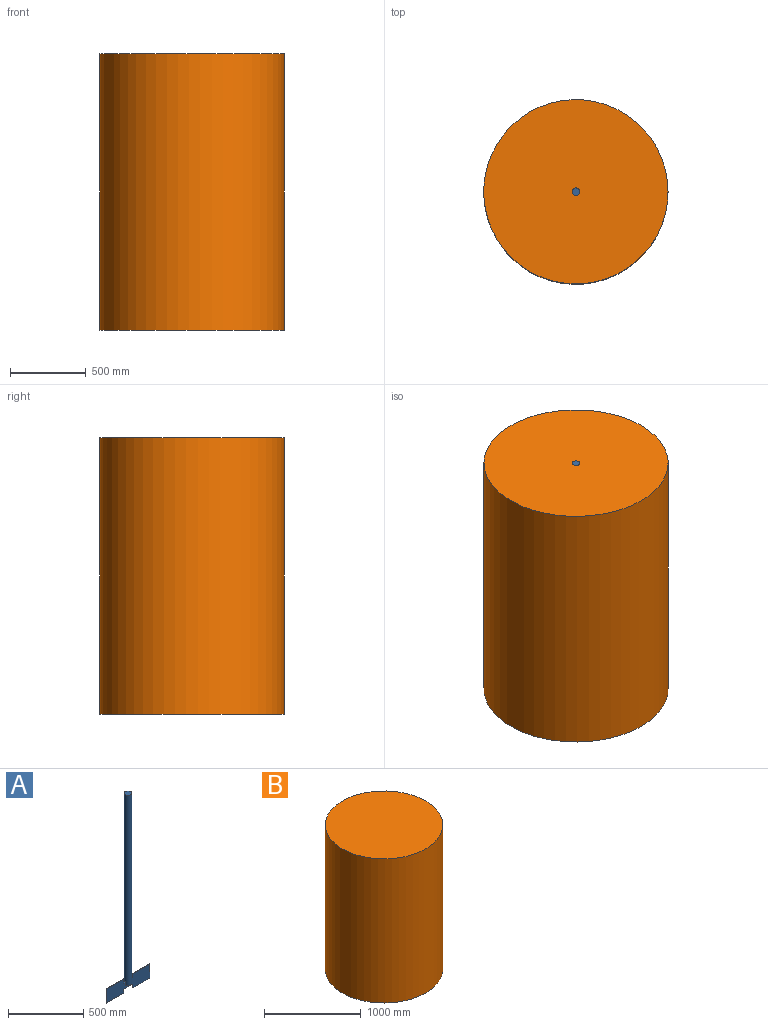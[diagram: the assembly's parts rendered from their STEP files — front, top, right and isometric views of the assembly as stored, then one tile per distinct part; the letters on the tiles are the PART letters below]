
ASSEMBLY  parts=2 mates=1
PART A: 19 faces, bbox 406.4x50.8x1606.1 mm
  f0: plane 17.68x6.35mm, normal (0,0,1), area 111.4mm2, adj f1,f2,f13,f16
  f1: plane 406.4x113.33mm, normal (0,-1,0), area 39414mm2, adj f0,f3,f4,f5,f6,f7,f8,f9
  f2: plane 406.4x113.33mm, normal (0,1,0), area 39414mm2, adj f0,f3,f4,f5,f6,f7,f8,f9
  f3: plane 31.26x6.35mm, normal (1,0,0), area 198.5mm2, adj f1,f2,f4,f14
  f4: plane 160.32x6.35mm, normal (0,0,1), area 1018mm2, adj f1,f2,f3,f5
  f5: plane 113.33x6.35mm, normal (-1,0,0), area 719.6mm2, adj f1,f2,f4,f6
  f6: plane 160.32x6.35mm, normal (0,0,-1), area 1018mm2, adj f1,f2,f5,f7
  f7: plane 31.26x6.35mm, normal (1,0,0), area 198.5mm2, adj f1,f2,f6,f8
  f8: plane 85.76x6.35mm, normal (0,0,-1), area 544.6mm2, adj f1,f2,f7,f9
  f9: plane 31.26x6.35mm, normal (-1,0,0), area 198.5mm2, adj f1,f2,f8,f10
  f10: plane 160.32x6.35mm, normal (0,0,-1), area 1018mm2, adj f1,f2,f9,f11
  f11: plane 113.33x6.35mm, normal (1,0,0), area 719.6mm2, adj f1,f2,f10,f12
  f12: plane 160.32x6.35mm, normal (0,0,1), area 1018mm2, adj f1,f2,f11,f13
  f13: plane 31.26x6.35mm, normal (-1,0,0), area 198.5mm2, adj f0,f1,f2,f12
  f14: plane 17.68x6.35mm, normal (0,0,1), area 111.4mm2, adj f1,f2,f3,f16
  f15: plane 50.4x22.23mm, normal (0,0,-1), area 852.5mm2, adj f2,f16
  f16: cylinder r=25.4mm len=1549.4mm, axis (0,0,-1), area 246949.8mm2, adj f0,f1,f2,f14,f15,f17,f18
  f17: plane 50.8x50.8mm, normal (0,0,1), area 2026.8mm2, adj f16
  f18: plane 50.4x22.23mm, normal (0,0,-1), area 852.5mm2, adj f1,f16
PART B: 3 faces, bbox 1219.2x1219.2x1828.8 mm
  f0: cylinder r=609.6mm len=1828.8mm, axis (0,0,-1), area 7004724.2mm2, adj f1,f2
  f1: plane 1219.2x1219.2mm, normal (0,0,1), area 1167454mm2, adj f0
  f2: plane 1219.2x1219.2mm, normal (0,0,-1), area 1167454mm2, adj f0
PLACE A t=(0,0,-635)mm
PLACE B at identity
MATE revolute A.f16 <-> B.f0  axis (0,0,1) through (0,0,914.4)mm
